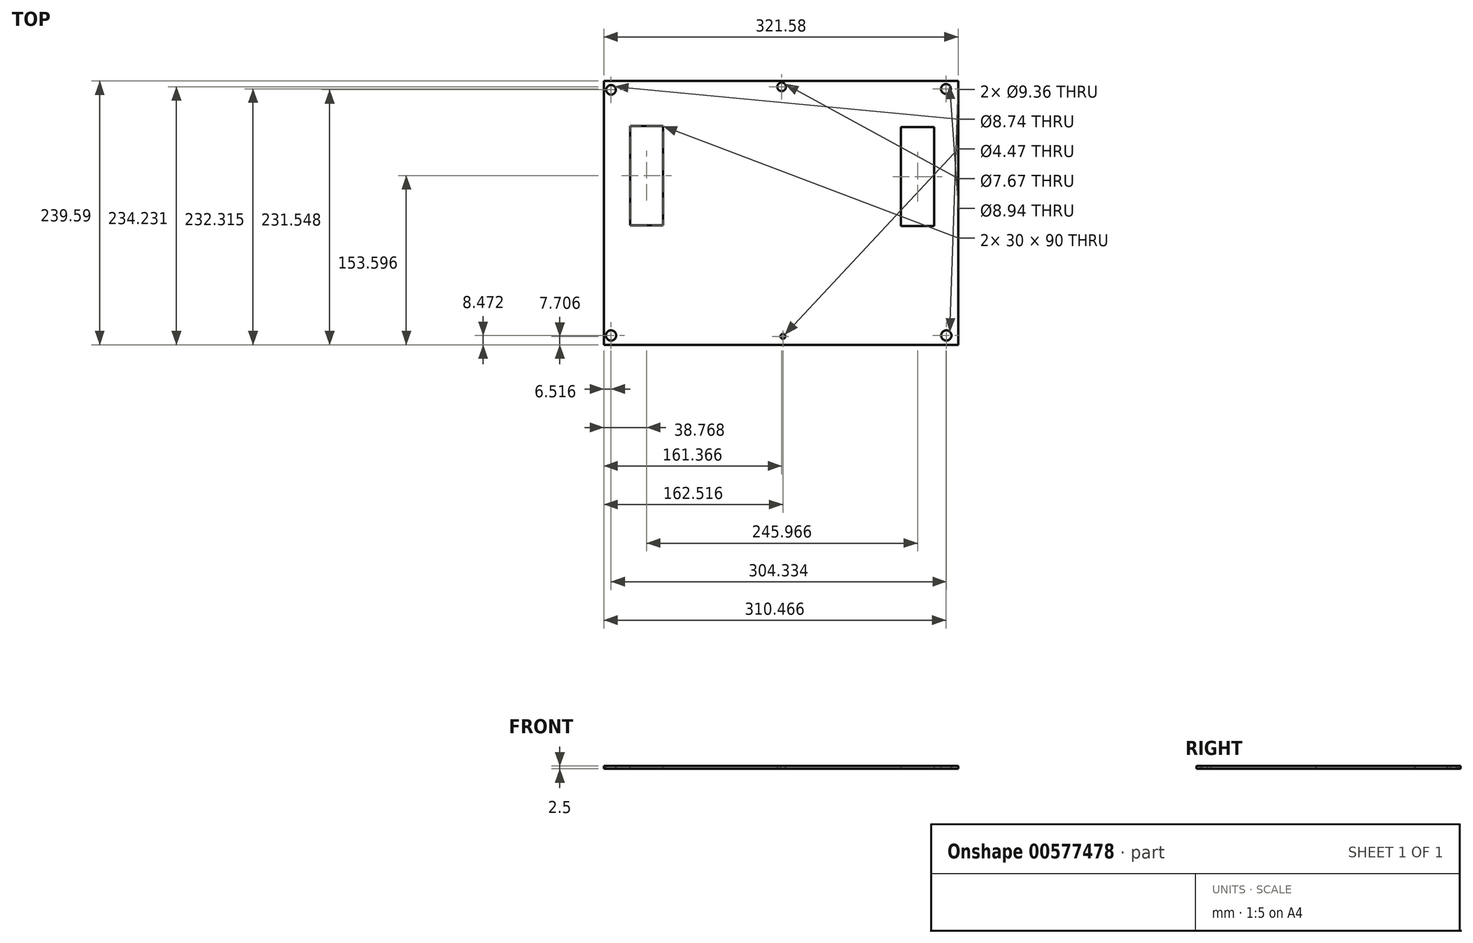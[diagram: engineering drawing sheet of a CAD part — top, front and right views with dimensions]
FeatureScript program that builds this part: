
annotation { "Feature Type Name" : "Feature", "Feature Type Description" : "" }
export const myFeature = defineFeature(function(context is Context, id is Id, definition is map)
    precondition{}
    {
        {
            var Q0;
            Q0=qCreatedBy(makeId("Top.planeOp"),FACE);
            var sketch = newSketch(context, id + "F0", { "sketchPlane" : qUnion([Q0])});
            skLineSegment(sketch, "E0.bottom", {"start": v(-170.02, 70.74) * mm, "end": v(151.56, 70.74) * mm});
            skLineSegment(sketch, "E0.top", {"start": v(-170.02, -168.85) * mm, "end": v(151.56, -168.85) * mm});
            skLineSegment(sketch, "E0.left", {"start": v(-170.02, 70.74) * mm, "end": v(-170.02, -168.85) * mm});
            skLineSegment(sketch, "E0.right", {"start": v(151.56, 70.74) * mm, "end": v(151.56, -168.85) * mm});
            skSolve(sketch);
        }
        {
            var Q0;
            Q0=qSketchRegion(id+"F0",true);
            extrude(context, id + "F1", {"entities" : qUnion([Q0]), "depth" : 2.5 * mm, "offsetDistance" : 25 * mm});
        }
        {
            var Q0;
            Q0=makeQuery(id+"F1.opExtrude","CAP_FACE",FACE,{"disambiguationData":[OSD([sQuery(id+"F0.wireOp",EDGE,"E0.bottom"),sQuery(id+"F0.wireOp",EDGE,"E0.top"),sQuery(id+"F0.wireOp",EDGE,"E0.left"),sQuery(id+"F0.wireOp",EDGE,"E0.right")])],"isStart":false});
            var sketch = newSketch(context, id + "F2", { "sketchPlane" : qUnion([Q0])});
            skLineSegment(sketch, "E1.bottom", {"start": v(-116.25, -60.25) * mm, "end": v(-146.25, -60.25) * mm});
            skLineSegment(sketch, "E1.top", {"start": v(-116.25, 29.75) * mm, "end": v(-146.25, 29.75) * mm});
            skLineSegment(sketch, "E1.left", {"start": v(-116.25, -60.25) * mm, "end": v(-116.25, 29.75) * mm});
            skLineSegment(sketch, "E1.right", {"start": v(-146.25, -60.25) * mm, "end": v(-146.25, 29.75) * mm});
            skSolve(sketch);
        }
        {
            var Q0;
            Q0=qSketchRegion(id+"F2",true);
            extrude(context, id + "F3", {"entities" : qUnion([Q0]), "operationType" : NewBodyOperationType.REMOVE, "oppositeDirection" : true, "depth" : 30 * mm, "offsetDistance" : 25 * mm});
        }
        {
            var Q0;
            Q0=qCreatedBy(makeId("Top.planeOp"),FACE);
            var sketch = newSketch(context, id + "F4", { "sketchPlane" : qUnion([Q0])});
            skLineSegment(sketch, "E2.bottom", {"start": v(129.71, -61.1) * mm, "end": v(99.71, -61.1) * mm});
            skLineSegment(sketch, "E2.top", {"start": v(129.71, 28.9) * mm, "end": v(99.71, 28.9) * mm});
            skLineSegment(sketch, "E2.left", {"start": v(129.71, -61.1) * mm, "end": v(129.71, 28.9) * mm});
            skLineSegment(sketch, "E2.right", {"start": v(99.71, -61.1) * mm, "end": v(99.71, 28.9) * mm});
            skSolve(sketch);
        }
        {
            var Q0;
            Q0=qSketchRegion(id+"F4",true);
            extrude(context, id + "F5", {"entities" : qUnion([Q0]), "operationType" : NewBodyOperationType.REMOVE, "oppositeDirection" : true, "depth" : -30 * mm, "offsetDistance" : 25 * mm});
        }
        {
            var Q0;
            Q0=makeQuery(id+"F2.imprint","IMPRINT",FACE,{"disambiguationData":[TD([[makeQuery(id+"F2.imprint","IMPRINT",EDGE,{"derivedFrom":sQuery(id+"F2.wireOp",EDGE,"E1.bottom")}),1.0]])]});
            var sketch = newSketch(context, id + "F6", { "sketchPlane" : qUnion([Q0])});
            skCircle(sketch, "E3", {"center": v(-163.5, 62.7) * mm, "radius": 4.37 * mm});
            skCircle(sketch, "E4", {"center": v(140.45, 63.46) * mm, "radius": 4.47 * mm});
            skCircle(sketch, "E5", {"center": v(-8.65, 65.38) * mm, "radius": 3.83 * mm});
            skCircle(sketch, "E6", {"center": v(-7.5, -161.14) * mm, "radius": 2.23 * mm});
            skCircle(sketch, "E7", {"center": v(-163.5, -160.38) * mm, "radius": 4.68 * mm});
            skCircle(sketch, "E8", {"center": v(140.83, -160.38) * mm, "radius": 4.68 * mm});
            skSolve(sketch);
        }
        {
            var Q0;
            Q0=qSketchRegion(id+"F6",true);
            extrude(context, id + "F7", {"entities" : qUnion([Q0]), "operationType" : NewBodyOperationType.REMOVE, "oppositeDirection" : true, "depth" : 30 * mm, "offsetDistance" : 25 * mm});
        }
    });
